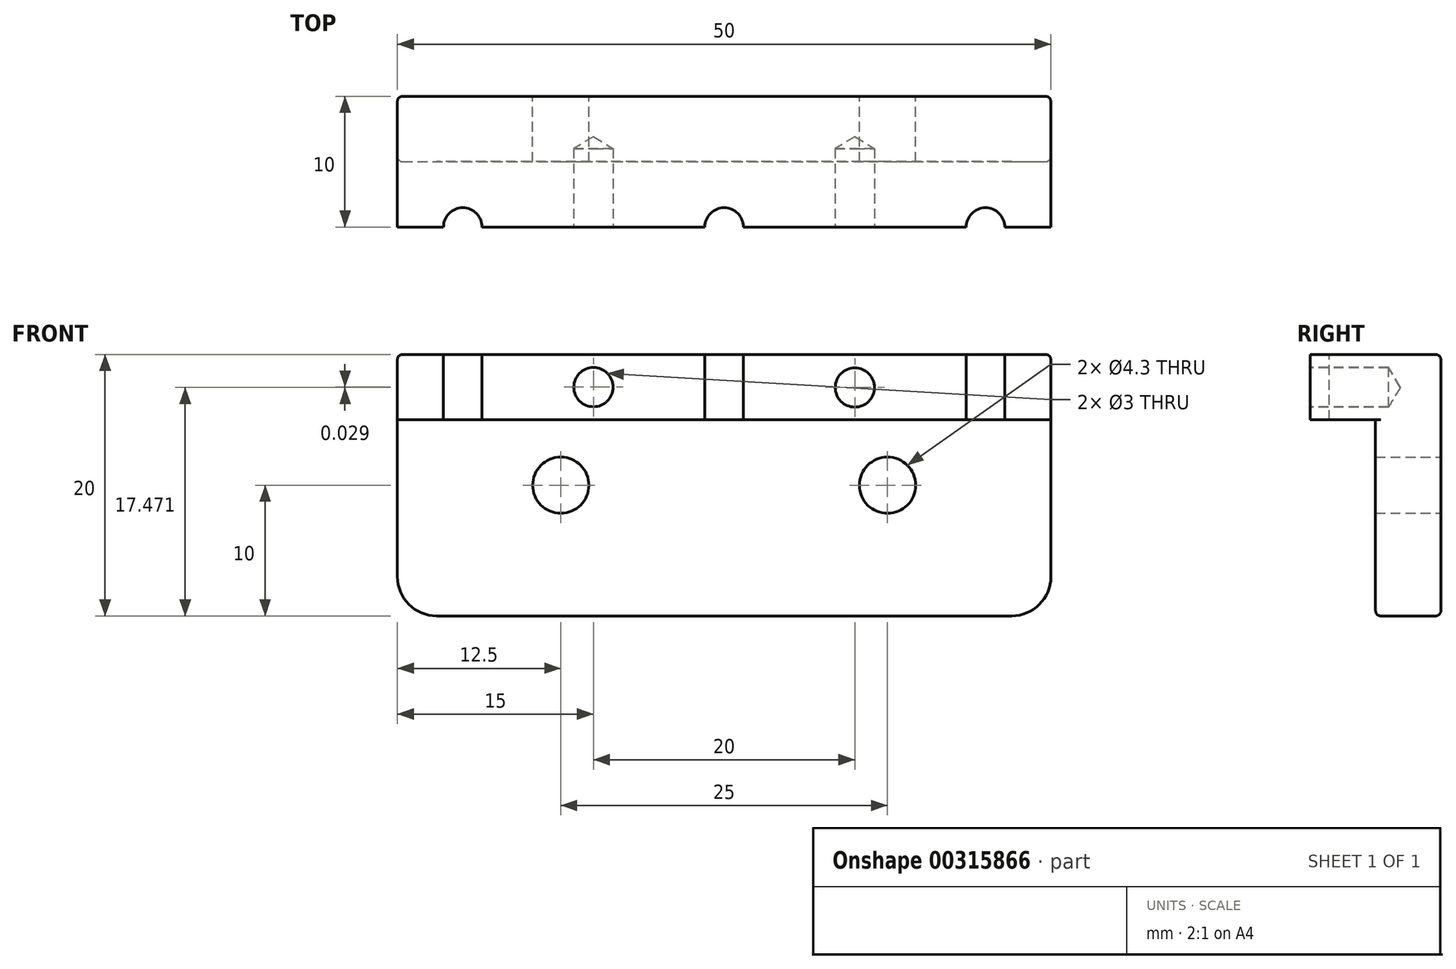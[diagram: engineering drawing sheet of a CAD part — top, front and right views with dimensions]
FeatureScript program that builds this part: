
annotation { "Feature Type Name" : "Feature", "Feature Type Description" : "" }
export const myFeature = defineFeature(function(context is Context, id is Id, definition is map)
    precondition{}
    {
        {
            var Q0;
            Q0=qCreatedBy(makeId("Front.planeOp"),FACE);
            var sketch = newSketch(context, id + "F0", { "sketchPlane" : qUnion([Q0])});
            skLineSegment(sketch, "E0.bottom", {"start": v(25, 10) * mm, "end": v(-25, 10) * mm});
            skLineSegment(sketch, "E0.top", {"start": v(25, -10) * mm, "end": v(-25, -10) * mm});
            skLineSegment(sketch, "E0.left", {"start": v(25, 10) * mm, "end": v(25, -10) * mm});
            skLineSegment(sketch, "E0.right", {"start": v(-25, 10) * mm, "end": v(-25, -10) * mm});
            skPoint(sketch, "E0.middle", {"position": v(0, 0) * mm});
            skPoint(sketch, "E1", {"position": v(-12.5, 0) * mm});
            skPoint(sketch, "E2", {"position": v(12.5, 0) * mm});
            skLineSegment(sketch, "E3", {"start": v(-25, 5) * mm, "end": v(25, 5) * mm});
            skSolve(sketch);
        }
        {
            var Q0;
            {var subQ0=sQuery(id+"F0.wireOp",EDGE,"E0.top");Q0=makeQuery(id+"F0.imprint","IMPRINT",FACE,{"disambiguationData":[TD([[makeQuery(id+"F0.imprint","IMPRINT",EDGE,{"derivedFrom":subQ0}),-1.0]])]});}
            extrude(context, id + "F1", {"entities" : qUnion([Q0]), "depth" : 5 * mm});
        }
        {
            var Q0;
            Q0=sQuery(id+"F0.wireOp",VERTEX,"E2");
            var Q1;
            Q1=sQuery(id+"F0.wireOp",VERTEX,"E1");
            var Q2;
            Q2=makeQuery(id+"F1.opExtrude","SWEPT_BODY",BODY,{"disambiguationData":[OSD([sQuery(id+"F0.wireOp",EDGE,"E0.bottom"),sQuery(id+"F0.wireOp",EDGE,"E0.top"),sQuery(id+"F0.wireOp",EDGE,"E0.left"),sQuery(id+"F0.wireOp",EDGE,"E0.right")])]});
            hole(context, id + "F2", {"style" : HoleStyle.SIMPLE, "endStyle" : HoleEndStyle.THROUGH, "oppositeDirection" : true, "holeDiameter" : 4.3 * mm, "isTappedThrough" : true, "tappedDepth" : 12 * mm, "tapClearance" : 3, "locations" : qUnion([Q0, Q1]), "scope" : qUnion([Q2])});
        }
        {
            var Q0;
            {var subQ0=sQuery(id+"F0.wireOp",EDGE,"E0.bottom");Q0=makeQuery(id+"F0.imprint","IMPRINT",FACE,{"disambiguationData":[TD([[makeQuery(id+"F0.imprint","IMPRINT",EDGE,{"derivedFrom":subQ0}),1.0]])]});}
            extrude(context, id + "F3", {"entities" : qUnion([Q0]), "operationType" : NewBodyOperationType.ADD, "depth" : 10 * mm});
        }
        {
            var Q0;
            Q0=makeQuery(id+"F3.opExtrude","SWEPT_FACE",FACE,{"disambiguationData":[OSD([sQuery(id+"F0.wireOp",EDGE,"E0.bottom")])]});
            var sketch = newSketch(context, id + "F4", { "sketchPlane" : qUnion([Q0])});
            skPoint(sketch, "E4", {"position": v(-20, -10) * mm});
            skPoint(sketch, "E5", {"position": v(0, -10) * mm});
            skPoint(sketch, "E6", {"position": v(20, -10) * mm});
            skSolve(sketch);
        }
        {
            var Q0;
            Q0=sQuery(id+"F4.wireOp",VERTEX,"E4");
            var Q1;
            Q1=sQuery(id+"F4.wireOp",VERTEX,"E5");
            var Q2;
            Q2=sQuery(id+"F4.wireOp",VERTEX,"E6");
            var Q3;
            Q3=makeQuery(id+"F1.opExtrude","SWEPT_BODY",BODY,{"disambiguationData":[OSD([sQuery(id+"F0.wireOp",EDGE,"E0.top"),sQuery(id+"F0.wireOp",EDGE,"E0.left"),sQuery(id+"F0.wireOp",EDGE,"E0.right"),sQuery(id+"F0.wireOp",EDGE,"E3")])]});
            hole(context, id + "F5", {"style" : HoleStyle.SIMPLE, "endStyle" : HoleEndStyle.THROUGH, "holeDiameter" : 2.95 * mm, "isTappedThrough" : true, "tappedDepth" : 12 * mm, "tapClearance" : 3, "locations" : qUnion([Q0, Q1, Q2]), "scope" : qUnion([Q3])});
        }
        {
            var Q0;
            Q0=makeQuery(id+"F1.opExtrude","SWEPT_EDGE",EDGE,{"disambiguationData":[OSD([sQuery(id+"F0.wireOp",EDGE,"E0.top"),sQuery(id+"F0.wireOp",EDGE,"E0.right")])]});
            var Q1;
            Q1=makeQuery(id+"F1.opExtrude","SWEPT_EDGE",EDGE,{"disambiguationData":[OSD([sQuery(id+"F0.wireOp",EDGE,"E0.top"),sQuery(id+"F0.wireOp",EDGE,"E0.left")])]});
            fillet(context, id + "F6", {"entities" : qUnion([Q0, Q1]), "radius" : 3 * mm, "tangentPropagation" : true, "allowEdgeOverflow" : false});
        }
        {
            var Q0;
            Q0=makeQuery(id+"F3.opExtrude","CAP_EDGE",EDGE,{"disambiguationData":[OSD([sQuery(id+"F0.wireOp",EDGE,"E0.bottom")])],"isStart":true});
            var Q1;
            {var subQ0=sQuery(id+"F0.wireOp",EDGE,"E0.right");Q1=makeQuery(id+"F3.boolean.opBoolean","MERGE",EDGE,{"derivedFrom":[makeQuery(id+"F1.opExtrude","CAP_EDGE",EDGE,{"disambiguationData":[OSD([subQ0])],"isStart":true}),makeQuery(id+"F3.opExtrude","CAP_EDGE",EDGE,{"disambiguationData":[OSD([subQ0])],"isStart":true})]});}
            var Q2;
            Q2=makeQuery(id+"F3.opExtrude","SWEPT_EDGE",EDGE,{"disambiguationData":[OSD([sQuery(id+"F0.wireOp",EDGE,"E0.bottom"),sQuery(id+"F0.wireOp",EDGE,"E0.right")])]});
            var Q3;
            Q3=makeQuery(id+"F3.opExtrude","SWEPT_EDGE",EDGE,{"disambiguationData":[OSD([sQuery(id+"F0.wireOp",EDGE,"E0.bottom"),sQuery(id+"F0.wireOp",EDGE,"E0.left")])]});
            var Q4;
            Q4=makeQuery(id+"F1.opExtrude","CAP_EDGE",EDGE,{"disambiguationData":[OSD([sQuery(id+"F0.wireOp",EDGE,"E0.top")])],"isStart":false});
            var Q5;
            Q5=makeQuery(id+"F1.opExtrude","CAP_EDGE",EDGE,{"disambiguationData":[OSD([sQuery(id+"F0.wireOp",EDGE,"E3")])],"isStart":false});
            fillet(context, id + "F7", {"entities" : qUnion([Q0, Q1, Q2, Q3, Q4, Q5]), "radius" : 0.4 * mm, "tangentPropagation" : true, "allowEdgeOverflow" : false});
        }
        {
            var Q0;
            {var subQ0=sQuery(id+"F0.wireOp",EDGE,"E0.bottom");var subQ2=sQuery(id+"F0.wireOp",EDGE,"E3");var subQ4=makeQuery(id+"F5.hole-0.opRevolve","SWEPT_FACE",FACE,{"disambiguationData":[OSD([sQuery(id+"F5.hole-0.sketch.wireOp",EDGE,"core_line_2")])]});var subQ5=sQuery(id+"F0.wireOp",EDGE,"E0.left");Q0=makeQuery(id+"F5.hole-1.boolean.opBoolean","SPLIT",FACE,{"disambiguationData":[TD([makeQuery(id+"F5.hole-0.boolean.opBoolean","COPY",FACE,{"derivedFrom":subQ4})])],"derivedFrom":makeQuery(id+"F5.hole-0.boolean.opBoolean","SPLIT",FACE,{"disambiguationData":[TD([makeQuery(id+"F1.opExtrude","SWEPT_FACE",FACE,{"disambiguationData":[OSD([subQ5])]})])],"derivedFrom":makeQuery(id+"F3.opExtrude","CAP_FACE",FACE,{"disambiguationData":[OSD([subQ0,subQ5,sQuery(id+"F0.wireOp",EDGE,"E0.right"),subQ2])],"isStart":false})})});}
            var sketch = newSketch(context, id + "F8", { "sketchPlane" : qUnion([Q0])});
            skPoint(sketch, "E7", {"position": v(-10, 7.5) * mm});
            skPoint(sketch, "E8", {"position": v(10, 7.47) * mm});
            skPoint(sketch, "E9", {"position": v(-10, 5) * mm});
            skSolve(sketch);
        }
        {
            var Q0;
            Q0=sQuery(id+"F8.wireOp",VERTEX,"E7");
            var Q1;
            Q1=sQuery(id+"F8.wireOp",VERTEX,"E8");
            var Q2;
            Q2=makeQuery(id+"F1.opExtrude","SWEPT_BODY",BODY,{"disambiguationData":[OSD([sQuery(id+"F0.wireOp",EDGE,"E0.top"),sQuery(id+"F0.wireOp",EDGE,"E0.left"),sQuery(id+"F0.wireOp",EDGE,"E0.right"),sQuery(id+"F0.wireOp",EDGE,"E3")])]});
            hole(context, id + "F9", {"style" : HoleStyle.SIMPLE, "endStyle" : HoleEndStyle.BLIND, "holeDiameter" : 3 * mm, "holeDepth" : 6 * mm, "isTappedThrough" : true, "tappedDepth" : 12 * mm, "tapClearance" : 3, "locations" : qUnion([Q0, Q1]), "scope" : qUnion([Q2])});
        }
    });
